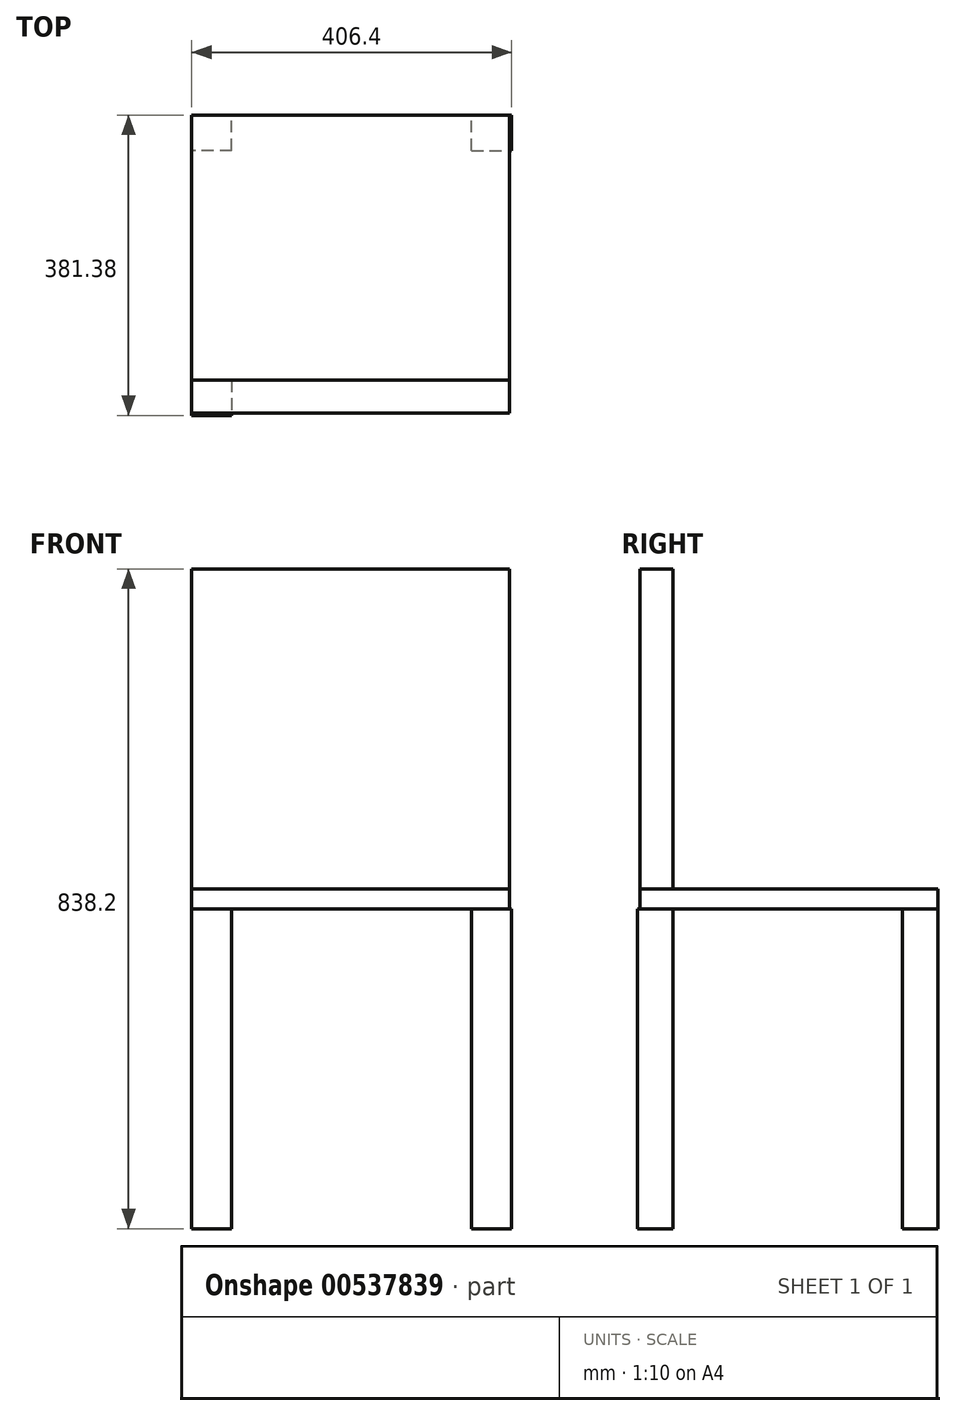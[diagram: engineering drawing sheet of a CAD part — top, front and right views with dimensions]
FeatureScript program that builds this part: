
annotation { "Feature Type Name" : "Feature", "Feature Type Description" : "" }
export const myFeature = defineFeature(function(context is Context, id is Id, definition is map)
    precondition{}
    {
        {
            var Q0;
            Q0=qCreatedBy(makeId("Top.planeOp"),FACE);
            var sketch = newSketch(context, id + "F0", { "sketchPlane" : qUnion([Q0])});
            skLineSegment(sketch, "E0", {"start": v(0, 0) * mm, "end": v(0, -44.85) * mm});
            skLineSegment(sketch, "E1", {"start": v(50.8, -44.85) * mm, "end": v(0, -44.85) * mm});
            skLineSegment(sketch, "E2", {"start": v(50.8, 0) * mm, "end": v(50.8, -44.85) * mm});
            skLineSegment(sketch, "E3", {"start": v(50.8, 0) * mm, "end": v(0, 0) * mm});
            skLineSegment(sketch, "E4", {"start": v(355.6, -22.43) * mm, "end": v(50.8, -22.43) * mm});
            skPoint(sketch, "E4.startSnap0", {"position": v(50.8, -22.43) * mm});
            skLineSegment(sketch, "E5", {"start": v(203.2, 282.37) * mm, "end": v(203.2, -22.43) * mm});
            skPoint(sketch, "E5.startSnap0", {"position": v(203.2, -22.43) * mm});
            skLineSegment(sketch, "E6.MirrorCS", {"start": v(355.6, 0) * mm, "end": v(406.4, 0) * mm});
            skLineSegment(sketch, "E7.MirrorCS", {"start": v(406.4, 0) * mm, "end": v(406.4, -44.85) * mm});
            skLineSegment(sketch, "E8.MirrorCS", {"start": v(355.6, -44.85) * mm, "end": v(406.4, -44.85) * mm});
            skLineSegment(sketch, "E9.MirrorCS", {"start": v(355.6, 0) * mm, "end": v(355.6, -44.85) * mm});
            skLineSegment(sketch, "E10", {"start": v(203.2, 145.84) * mm, "end": v(91.65, 145.84) * mm});
            skLineSegment(sketch, "E11", {"start": v(203.2, 282.37) * mm, "end": v(264.52, 282.37) * mm});
            skLineSegment(sketch, "E12", {"start": v(264.52, 282.37) * mm, "end": v(264.52, -22.43) * mm});
            skLineSegment(sketch, "E13.MirrorCS", {"start": v(355.6, 291.68) * mm, "end": v(406.4, 291.68) * mm});
            skLineSegment(sketch, "E14.MirrorCS", {"start": v(355.6, 336.53) * mm, "end": v(406.4, 336.53) * mm});
            skLineSegment(sketch, "E15.MirrorCS", {"start": v(406.4, 291.68) * mm, "end": v(406.4, 336.53) * mm});
            skLineSegment(sketch, "E16.MirrorCS", {"start": v(355.6, 291.68) * mm, "end": v(355.6, 336.53) * mm});
            skLineSegment(sketch, "E17.MirrorCS", {"start": v(50.8, 291.68) * mm, "end": v(0, 291.68) * mm});
            skLineSegment(sketch, "E18.MirrorCS", {"start": v(50.8, 291.68) * mm, "end": v(50.8, 336.53) * mm});
            skLineSegment(sketch, "E19.MirrorCS", {"start": v(50.8, 336.53) * mm, "end": v(0, 336.53) * mm});
            skLineSegment(sketch, "E20.MirrorCS", {"start": v(0, 291.68) * mm, "end": v(0, 336.53) * mm});
            skSolve(sketch);
        }
        {
            var Q0;
            Q0=makeQuery(id+"F0.imprint","IMPRINT",FACE,{"disambiguationData":[TD([[makeQuery(id+"F0.imprint","IMPRINT",EDGE,{"derivedFrom":sQuery(id+"F0.wireOp",EDGE,"E0")}),1.0]])]});
            var Q1;
            Q1=makeQuery(id+"F0.imprint","IMPRINT",FACE,{"disambiguationData":[TD([[makeQuery(id+"F0.imprint","IMPRINT",EDGE,{"derivedFrom":sQuery(id+"F0.wireOp",EDGE,"E13.MirrorCS")}),1.0]])]});
            var Q2;
            Q2=makeQuery(id+"F0.imprint","IMPRINT",FACE,{"disambiguationData":[TD([[makeQuery(id+"F0.imprint","IMPRINT",EDGE,{"derivedFrom":sQuery(id+"F0.wireOp",EDGE,"E7.MirrorCS")}),-1.0]])]});
            var Q3;
            Q3=makeQuery(id+"F0.imprint","IMPRINT",FACE,{"disambiguationData":[TD([[makeQuery(id+"F0.imprint","IMPRINT",EDGE,{"derivedFrom":sQuery(id+"F0.wireOp",EDGE,"E17.MirrorCS")}),-1.0]])]});
            extrude(context, id + "F1", {"entities" : qUnion([Q0, Q1, Q2, Q3]), "depth" : 406.4 * mm, "offsetDistance" : 25.4 * mm});
        }
        {
            var Q0;
            Q0=makeQuery(id+"F1.opExtrude","CAP_FACE",FACE,{"disambiguationData":[OSD([sQuery(id+"F0.wireOp",EDGE,"E17.MirrorCS"),sQuery(id+"F0.wireOp",EDGE,"E18.MirrorCS"),sQuery(id+"F0.wireOp",EDGE,"E19.MirrorCS"),sQuery(id+"F0.wireOp",EDGE,"E20.MirrorCS")])],"isStart":false});
            var sketch = newSketch(context, id + "F2", { "sketchPlane" : qUnion([Q0])});
            skLineSegment(sketch, "E21", {"start": v(0, 336.53) * mm, "end": v(0, -42.06) * mm});
            skLineSegment(sketch, "E22", {"start": v(0, -42.06) * mm, "end": v(403.88, -42.06) * mm});
            skLineSegment(sketch, "E23", {"start": v(403.88, -42.06) * mm, "end": v(403.88, 336.53) * mm});
            skLineSegment(sketch, "E24", {"start": v(403.88, 336.53) * mm, "end": v(0, 336.53) * mm});
            skSolve(sketch);
        }
        {
            var Q0;
            {var subQ3=sQuery(id+"F2.wireOp",EDGE,"E22");Q0=makeQuery(id+"F2.imprint","IMPRINT",FACE,{"disambiguationData":[TD([[makeQuery(id+"F2.imprint","IMPRINT",EDGE,{"derivedFrom":subQ3}),1.0]])]});}
            var Q1;
            {var subQ1=makeQuery(id+"F1.opExtrude","CAP_EDGE",EDGE,{"disambiguationData":[OSD([sQuery(id+"F0.wireOp",EDGE,"E17.MirrorCS")])],"isStart":false});Q1=makeQuery(id+"F2.imprint","IMPRINT",FACE,{"disambiguationData":[TD([[makeQuery(id+"F2.imprint","IMPRINT",EDGE,{"derivedFrom":subQ1}),-1.0]])]});}
            extrude(context, id + "F3", {"entities" : qUnion([Q0, Q1]), "depth" : 25.4 * mm, "offsetDistance" : 25.4 * mm});
        }
        {
            var Q0;
            Q0=makeQuery(id+"F3.opExtrude","CAP_FACE",FACE,{"disambiguationData":[OSD([sQuery(id+"F0.wireOp",EDGE,"E17.MirrorCS"),sQuery(id+"F0.wireOp",EDGE,"E18.MirrorCS"),sQuery(id+"F2.wireOp",EDGE,"E21"),sQuery(id+"F2.wireOp",EDGE,"E22"),sQuery(id+"F2.wireOp",EDGE,"E23"),sQuery(id+"F2.wireOp",EDGE,"E24")])],"isStart":false});
            var sketch = newSketch(context, id + "F4", { "sketchPlane" : qUnion([Q0])});
            skLineSegment(sketch, "E25", {"start": v(0, 0) * mm, "end": v(403.88, 0) * mm});
            skSolve(sketch);
        }
        {
            var Q0;
            Q0 = qSketchRegion(id + "F4", true);
            var Q1;
            Q1=makeQuery(id+"F4.imprint","IMPRINT",FACE,{"disambiguationData":[TD([[makeQuery(id+"F4.imprint","IMPRINT",EDGE,{"derivedFrom":sQuery(id+"F4.wireOp",EDGE,"wjDf9b2I-YnD8-diY2-G0HY-8ZpjZDPOybVA")}),1.0]])]});
            var Q2;
            {var subQ0=sQuery(id+"F4.wireOp",EDGE,"lSKYDA7i-aZsL-dbg2-JJ4J-pzkQeSlb6zkS");Q2=makeQuery(id+"F4.imprint","IMPRINT",FACE,{"disambiguationData":[TD([[makeQuery(id+"F4.imprint","IMPRINT",EDGE,{"derivedFrom":subQ0}),1.0]])]});}
            var Q3;
            {var subQ0=sQuery(id+"F4.wireOp",EDGE,"E25");Q3=makeQuery(id+"F4.imprint","IMPRINT",FACE,{"disambiguationData":[TD([[makeQuery(id+"F4.imprint","IMPRINT",EDGE,{"derivedFrom":subQ0}),-1.0]])]});}
            extrude(context, id + "F5", {"entities" : qUnion([Q0, Q1, Q2, Q3]), "depth" : 406.4 * mm, "offsetDistance" : 25.4 * mm});
        }
    });
